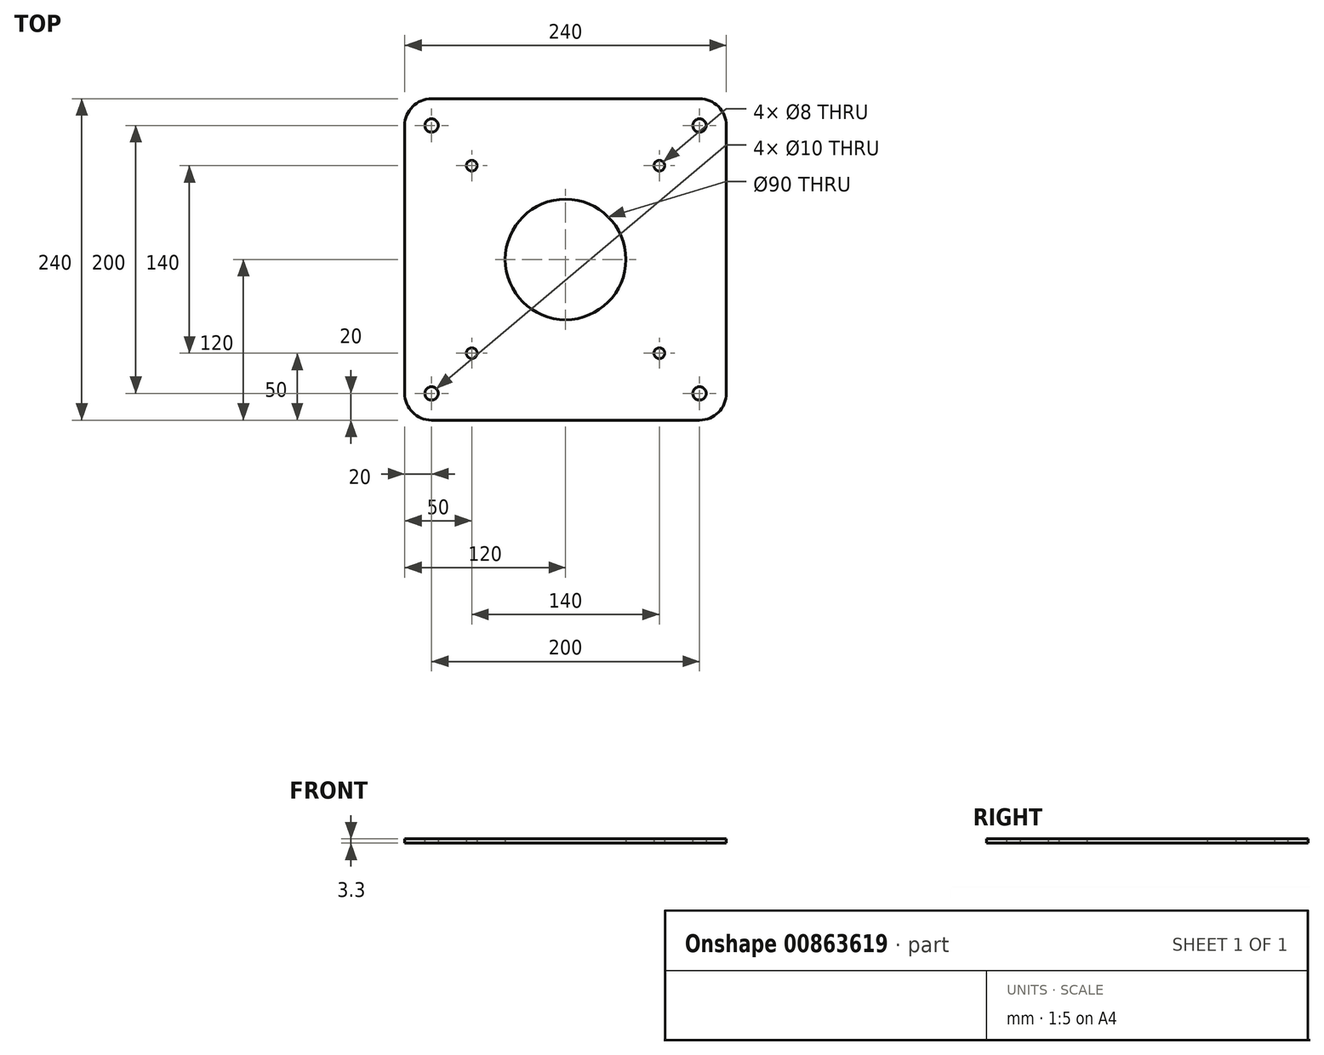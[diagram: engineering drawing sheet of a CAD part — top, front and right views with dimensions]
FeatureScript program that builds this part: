
annotation { "Feature Type Name" : "Feature", "Feature Type Description" : "" }
export const myFeature = defineFeature(function(context is Context, id is Id, definition is map)
    precondition{}
    {
        {
            var Q0;
            Q0=qCreatedBy(makeId("Top.planeOp"),FACE);
            var sketch = newSketch(context, id + "F0", { "sketchPlane" : qUnion([Q0])});
            skCircle(sketch, "E0", {"center": v(0, 0) * mm, "radius": 4 * mm});
            skCircle(sketch, "E1", {"center": v(-30, -30) * mm, "radius": 5 * mm});
            skCircle(sketch, "E2.0.1.0", {"center": v(0, 140) * mm, "radius": 4 * mm});
            skCircle(sketch, "E2.1.0.0", {"center": v(140, 0) * mm, "radius": 4 * mm});
            skCircle(sketch, "E2.1.1.0", {"center": v(140, 140) * mm, "radius": 4 * mm});
            skLineSegment(sketch, "E2.direction1", {"start": v(0, 0) * mm, "end": v(140, 0) * mm, "construction": true});
            skLineSegment(sketch, "E2.direction2", {"start": v(0, 0) * mm, "end": v(0, 140) * mm, "construction": true});
            skCircle(sketch, "E3.0.1.0", {"center": v(-30, 170) * mm, "radius": 5 * mm});
            skCircle(sketch, "E3.1.0.0", {"center": v(170, -30) * mm, "radius": 5 * mm});
            skCircle(sketch, "E3.1.1.0", {"center": v(170, 170) * mm, "radius": 5 * mm});
            skLineSegment(sketch, "E3.direction1", {"start": v(-30, -30) * mm, "end": v(170, -30) * mm, "construction": true});
            skLineSegment(sketch, "E3.direction2", {"start": v(-30, -30) * mm, "end": v(-30, 170) * mm, "construction": true});
            skLineSegment(sketch, "E4.bottom", {"start": v(-30, 190) * mm, "end": v(170, 190) * mm});
            skLineSegment(sketch, "E4.top", {"start": v(-30, -50) * mm, "end": v(170, -50) * mm});
            skLineSegment(sketch, "E4.left", {"start": v(-50, 170) * mm, "end": v(-50, -30) * mm});
            skLineSegment(sketch, "E4.right", {"start": v(190, 170) * mm, "end": v(190, -30) * mm});
            skPoint(sketch, "E5.visualSharp", {"position": v(-50, 190) * mm});
            skArc(sketch, "E5.filletArc", {"start": v(-30, 190) * mm, "mid": v(-44.14, 184.14) * mm, "end": v(-50, 170) * mm});
            skPoint(sketch, "E6.visualSharp", {"position": v(190, 190) * mm});
            skArc(sketch, "E6.filletArc", {"start": v(190, 170) * mm, "mid": v(184.14, 184.14) * mm, "end": v(170, 190) * mm});
            skPoint(sketch, "E7.visualSharp", {"position": v(190, -50) * mm});
            skArc(sketch, "E7.filletArc", {"start": v(170, -50) * mm, "mid": v(184.14, -44.14) * mm, "end": v(190, -30) * mm});
            skPoint(sketch, "E8.visualSharp", {"position": v(-50, -50) * mm});
            skArc(sketch, "E8.filletArc", {"start": v(-50, -30) * mm, "mid": v(-44.14, -44.14) * mm, "end": v(-30, -50) * mm});
            skCircle(sketch, "E9", {"center": v(70, 70) * mm, "radius": 45 * mm});
            skSolve(sketch);
        }
        {
            var Q0;
            Q0=makeQuery(id+"F0.imprint","IMPRINT",FACE,{"disambiguationData":[TD([[makeQuery(id+"F0.imprint","IMPRINT",EDGE,{"derivedFrom":sQuery(id+"F0.wireOp",EDGE,"E0")}),-1.0]])]});
            extrude(context, id + "F1", {"entities" : qUnion([Q0]), "depth" : 3.3 * mm, "offsetDistance" : 25 * mm});
        }
    });
